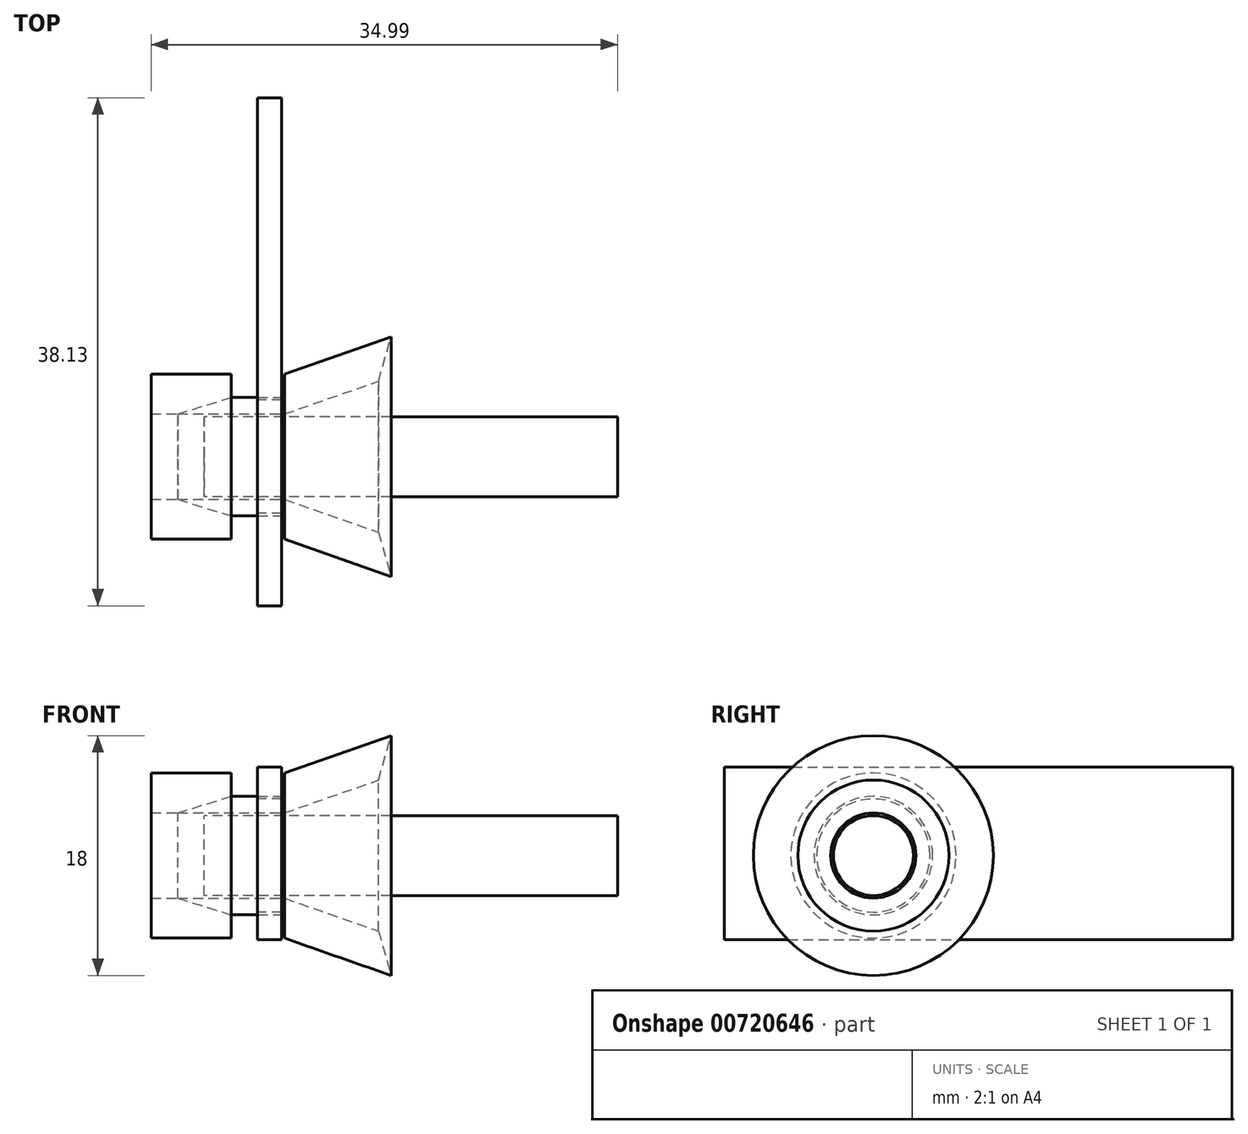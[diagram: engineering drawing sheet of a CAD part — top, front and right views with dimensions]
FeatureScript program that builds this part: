
annotation { "Feature Type Name" : "Feature", "Feature Type Description" : "" }
export const myFeature = defineFeature(function(context is Context, id is Id, definition is map)
    precondition{}
    {
        {
            var Q0;
            Q0=qCreatedBy(makeId("Right.planeOp"),FACE);
            var sketch = newSketch(context, id + "F0", { "sketchPlane" : qUnion([Q0])});
            skCircle(sketch, "E0", {"center": v(0, 0) * mm, "radius": 3 * mm});
            skSolve(sketch);
        }
        {
            var Q0;
            Q0 = qSketchRegion(id + "F0", true);
            extrude(context, id + "F1", {"entities" : qUnion([Q0]), "depth" : 31 * mm, "offsetDistance" : 25 * mm});
        }
        {
            var Q0;
            Q0=qCreatedBy(makeId("Right.planeOp"),FACE);
            cPlane(context, id + "F2", {"entities" : qUnion([Q0]), "cplaneType" : CPlaneType.OFFSET, "offset" : 4 * mm, "width" : 150 * mm, "height" : 150 * mm});
        }
        {
            var Q0;
            Q0=qCreatedBy(id+"F2.planeOp",FACE);
            var sketch = newSketch(context, id + "F3", { "sketchPlane" : qUnion([Q0])});
            skLineSegment(sketch, "E1.bottom", {"start": v(-11.2, 6.63) * mm, "end": v(26.94, 6.63) * mm});
            skLineSegment(sketch, "E1.top", {"start": v(-11.2, -6.32) * mm, "end": v(26.94, -6.32) * mm});
            skLineSegment(sketch, "E1.left", {"start": v(-11.2, 6.63) * mm, "end": v(-11.2, -6.32) * mm});
            skLineSegment(sketch, "E1.right", {"start": v(26.94, 6.63) * mm, "end": v(26.94, -6.32) * mm});
            skCircle(sketch, "E2", {"center": v(0, 0) * mm, "radius": 4.25 * mm});
            skSolve(sketch);
        }
        {
            var Q0;
            Q0 = qSketchRegion(id + "F3", true);
            extrude(context, id + "F4", {"entities" : qUnion([Q0]), "depth" : 1.8 * mm, "offsetDistance" : 25 * mm});
        }
        {
            var Q0;
            Q0=qCreatedBy(makeId("Front.planeOp"),FACE);
            var sketch = newSketch(context, id + "F5", { "sketchPlane" : qUnion([Q0])});
            skLineSegment(sketch, "E3", {"start": v(14.01, 6) * mm, "end": v(14.01, 0) * mm, "construction": true});
            skLineSegment(sketch, "E4", {"start": v(14.01, 0) * mm, "end": v(0, 0) * mm, "construction": true});
            skLineSegment(sketch, "E5", {"start": v(0, 0) * mm, "end": v(0, 2.8) * mm});
            skLineSegment(sketch, "E6", {"start": v(14.01, 6) * mm, "end": v(14.01, 9) * mm});
            skLineSegment(sketch, "E7", {"start": v(14.01, 6) * mm, "end": v(6.01, 3.2) * mm});
            skLineSegment(sketch, "E8", {"start": v(6.01, 3.2) * mm, "end": v(-0.81, 3.2) * mm});
            skLineSegment(sketch, "E9", {"start": v(-3.99, 3.2) * mm, "end": v(-3.99, 6.2) * mm});
            skLineSegment(sketch, "E10", {"start": v(-3.99, 6.2) * mm, "end": v(2.01, 6.2) * mm});
            skLineSegment(sketch, "E11", {"start": v(2.01, 6.2) * mm, "end": v(2.01, 4.45) * mm});
            skLineSegment(sketch, "E12", {"start": v(-0.81, 0) * mm, "end": v(0, 0) * mm});
            skPoint(sketch, "E13.endSnap0", {"position": v(-1, 0) * mm});
            skPoint(sketch, "E14.trimOffspring.end.orphan", {"position": v(3.72, 3.2) * mm});
            skLineSegment(sketch, "E15", {"start": v(-0.81, 3.2) * mm, "end": v(-3.99, 3.2) * mm});
            skPoint(sketch, "E13.end.orphan", {"position": v(-0.81, 0) * mm});
            skPoint(sketch, "E16.orphan", {"position": v(-2, 0) * mm});
            skLineSegment(sketch, "E17", {"start": v(14.01, 9) * mm, "end": v(6.01, 6.2) * mm});
            skLineSegment(sketch, "E18", {"start": v(0, 3) * mm, "end": v(14.61, 3) * mm, "construction": true});
            skLineSegment(sketch, "E19", {"start": v(6.01, 4.45) * mm, "end": v(-7.11, 4.45) * mm, "construction": true});
            skLineSegment(sketch, "E20", {"start": v(6.01, 4.45) * mm, "end": v(2.01, 4.45) * mm});
            skLineSegment(sketch, "E21", {"start": v(6.01, 6.2) * mm, "end": v(6.01, 4.45) * mm});
            skLineSegment(sketch, "E22", {"start": v(1.02, 6.2) * mm, "end": v(7.05, 6.2) * mm, "construction": true});
            skLineSegment(sketch, "E23", {"start": v(2.01, 4.45) * mm, "end": v(-1.99, 3.2) * mm});
            skSolve(sketch);
        }
        {
            var Q0;
            Q0=makeQuery(id+"F5.imprint","IMPRINT",FACE,{"disambiguationData":[TD([[makeQuery(id+"F5.imprint","IMPRINT",EDGE,{"derivedFrom":sQuery(id+"F5.wireOp",EDGE,"E6")}),1.0]])]});
            var Q1;
            Q1=sQuery(id+"F5.wireOp",EDGE,"E4");
            revolve(context, id + "F6", {"surfaceOperationType" : NewSurfaceOperationType.NEW, "entities" : qUnion([Q0]), "axis" : qUnion([Q1]), "revolveType" : RevolveType.FULL});
        }
        {
            var Q0;
            Q0=makeQuery(id+"F6.opRevolve","SWEPT_EDGE",EDGE,{"disambiguationData":[OSD([sQuery(id+"F5.wireOp",EDGE,"E6"),sQuery(id+"F5.wireOp",EDGE,"E7")])]});
            chamfer(context, id + "F7", {"entities" : qUnion([Q0]), "chamferType" : ChamferType.TWO_OFFSETS, "width1" : 3 * mm, "oppositeDirection" : false, "width2" : 1 * mm, "tangentPropagation" : true});
        }
        {
            var Q0;
            Q0=makeQuery(id+"F5.imprint","IMPRINT",FACE,{"disambiguationData":[TD([[makeQuery(id+"F5.imprint","IMPRINT",EDGE,{"derivedFrom":sQuery(id+"F5.wireOp",EDGE,"E9")}),-1.0]])]});
            var Q1;
            Q1=sQuery(id+"F5.wireOp",EDGE,"E4");
            revolve(context, id + "F8", {"surfaceOperationType" : NewSurfaceOperationType.NEW, "entities" : qUnion([Q0]), "axis" : qUnion([Q1]), "revolveType" : RevolveType.FULL});
        }
    });
